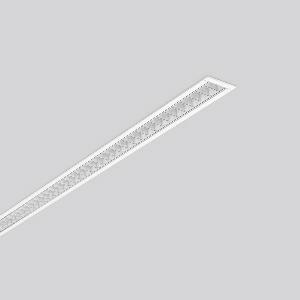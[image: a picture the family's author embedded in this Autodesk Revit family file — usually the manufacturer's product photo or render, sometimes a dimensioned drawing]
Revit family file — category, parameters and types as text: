
# Revit family: less_is_more_27_312177_002_1_76_c780
name_source: partatom
category: Lighting Fixtures
units: mm (PartAtom-declared; Revit-internal decimal feet)

## family parameters
Cut with Voids When Loaded = No
Host = Face
Light Source = No
Part Type = Normal
Room Calculation Point = No
Round Connector Dimension = Use Diameter
Shared = No

## types (1)
- LESS IS MORE 27 (1 x LED Modul 840, 2350 lm, 4000)
    Apparent Load = 25 VA
    CIE Flux Codes = 90 99 100 100 100
    Color Rendering = 80
    Color Temperature = 4000
    Default Elevation = 1800 mm
    Description = Series: LESS IS MORE 27
Recessed ceiling and wall luminaire with slim design. Housing: extruded aluminium profile, powder-coated. End cap aluminium powder-coated. High polish aluminium micro grid. Perfect for office areas (RUG < 19) and environments with computer screens in accordance with EN 12464-1. Suitable for Recessed ceiling mounting, wall (recessed). External driver with connecting cable. 
Colour: traffic white, matt (RAL 9016)
Length: 1014 mm
Width: 38 mm
Height: 2 mm
Cut-out length: 1006 mm
Cut-out width: 30 mm
Recess height: 45-60 mm
Luminaire: recess height: 37 mm
Lamp: LED
Socket: without socket
Colour temperature: 4000K
Colour rendering index (CRI): 82
System power: 25 W
Rated luminous flux: 2350 lm
Luminous efficiency: 94 lm/W
Control gear: Voltage converter, DALI dim.
Protection class: II
Type of protection: IP 20
    Height = 0 mm  [stored 0 ft]
    Lamp = 1 x LED Modul 840
    Lamp Light Flux = 2350 lm
    Lamp count = 1
    Length = 1014 mm
    Lifetime = 50000 h
    Luminous efficacy = 94 lm/W
    Manufacturer = RZB
    ModVariant = No
    Model = 312177.002.1.76
    Mounting Place = Ceiling, Wall
    Mounting Type = Recessed
    Number of Poles = 1
    OnlyDefault = Yes
    Power Factor = 1
    Product Name = LESS IS MORE 27
    Product group = Recessed LED linear luminaires
    ProductGroupID = 407
    Protection Class = Protection class II
    Protection Degree = IP 20
    RLX_Detail_Level = 1
    RLX_Emergency_Light_Flux = 0 lm
    RLX_Emergency_Type = 0
    RLX_Emergency_Type_DB = No
    RlxData = <blob elided: 27025 chars, md5=b3de7a89>
    Socket = socket
    Standby Power = 0 W
    System Light Flux = 2350 lm
    System Power = 25 W
    Type Comments = Product without accessories
    Type Image = 312177.002.jpg
    URL = http://relux.com
    VarID = ---
    Voltage = 230 V
    Voltage Range = 220-240 V
    Weight = 0.00 kg
    Width = 38 mm

note: [stored X ft] marks values corroborated as IEEE doubles in the binary element streams (Revit-internal decimal feet)

## geometry (parser evidence)
native form markers: Blend x4, Sweep x11
no freeform markers — native parametric forms only
